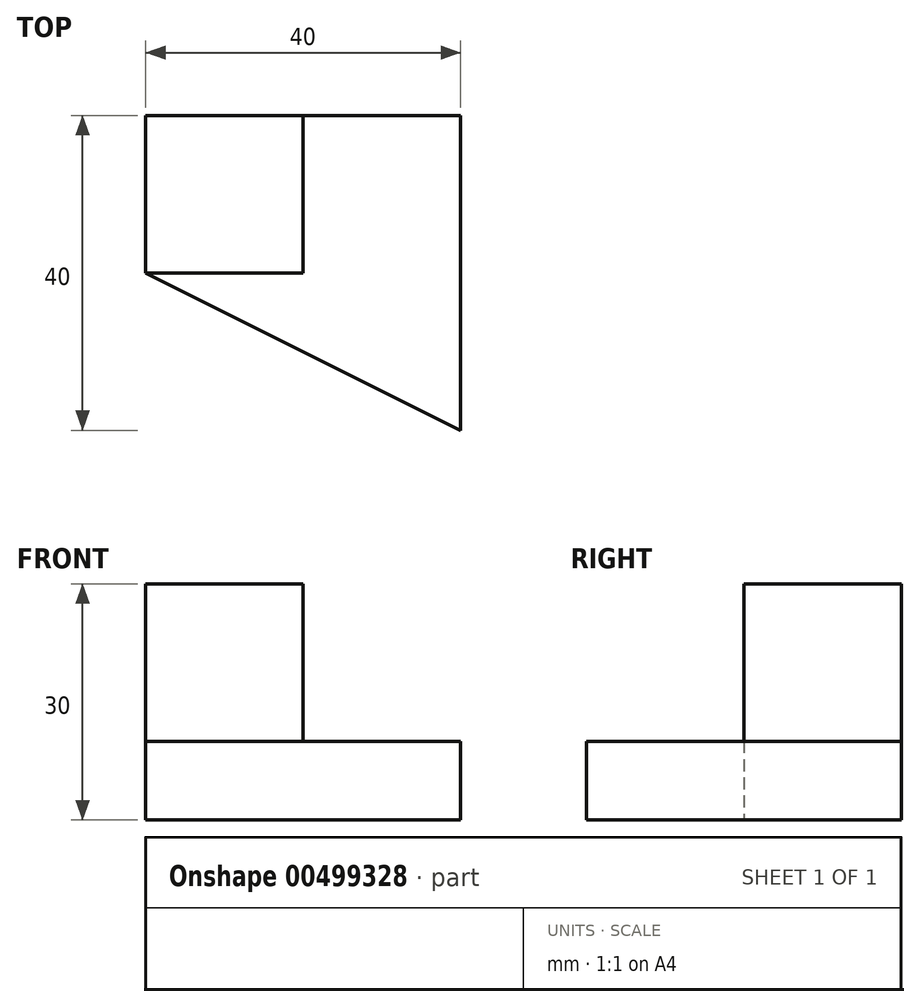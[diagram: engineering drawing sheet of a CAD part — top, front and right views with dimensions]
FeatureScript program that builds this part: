
annotation { "Feature Type Name" : "Feature", "Feature Type Description" : "" }
export const myFeature = defineFeature(function(context is Context, id is Id, definition is map)
    precondition{}
    {
        {
            var Q0;
            Q0=qCreatedBy(makeId("Top.planeOp"),FACE);
            var sketch = newSketch(context, id + "F0", { "sketchPlane" : qUnion([Q0])});
            skLineSegment(sketch, "E0", {"start": v(0, 0) * mm, "end": v(0, 20) * mm});
            skLineSegment(sketch, "E1", {"start": v(0, 20) * mm, "end": v(40, 20) * mm});
            skLineSegment(sketch, "E2", {"start": v(40, 20) * mm, "end": v(40, -20) * mm});
            skLineSegment(sketch, "E3", {"start": v(0, 0) * mm, "end": v(40, -20) * mm});
            skSolve(sketch);
        }
        {
            var Q0;
            Q0 = qSketchRegion(id + "F0", true);
            extrude(context, id + "F1", {"entities" : qUnion([Q0]), "depth" : 10 * mm});
        }
        {
            var Q0;
            Q0=makeQuery(id+"F1.opExtrude","CAP_FACE",FACE,{"disambiguationData":[OSD([sQuery(id+"F0.wireOp",EDGE,"E0"),sQuery(id+"F0.wireOp",EDGE,"E1"),sQuery(id+"F0.wireOp",EDGE,"E2"),sQuery(id+"F0.wireOp",EDGE,"E3")])],"isStart":false});
            var sketch = newSketch(context, id + "F2", { "sketchPlane" : qUnion([Q0])});
            skLineSegment(sketch, "E4", {"start": v(40, 20) * mm, "end": v(0, 20) * mm});
            skLineSegment(sketch, "E5", {"start": v(0, 20) * mm, "end": v(0, 0) * mm});
            skLineSegment(sketch, "E6", {"start": v(0, 0) * mm, "end": v(20, 0) * mm});
            skPoint(sketch, "E6.endSnap0", {"position": v(40, 0) * mm});
            skLineSegment(sketch, "E7", {"start": v(20, 0) * mm, "end": v(20, 20) * mm});
            skSolve(sketch);
        }
        {
            var Q0;
            Q0 = qSketchRegion(id + "F2", true);
            extrude(context, id + "F3", {"entities" : qUnion([Q0]), "operationType" : NewBodyOperationType.ADD, "depth" : 20 * mm});
        }
    });
